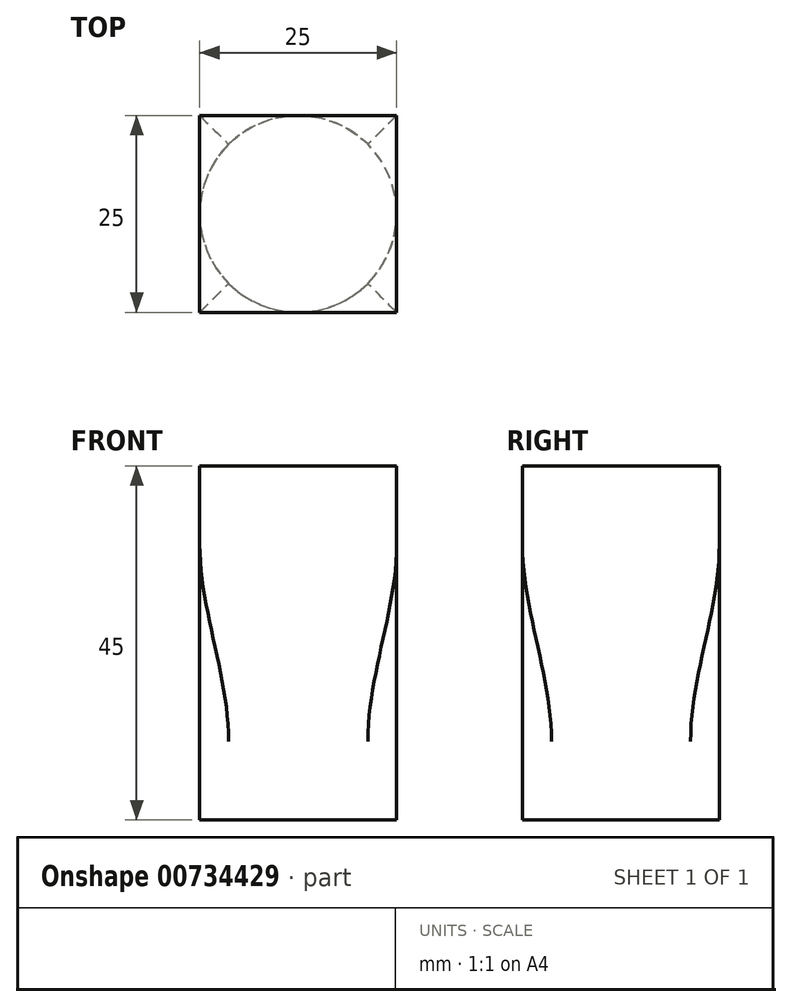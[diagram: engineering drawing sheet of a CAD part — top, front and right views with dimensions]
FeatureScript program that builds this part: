
annotation { "Feature Type Name" : "Feature", "Feature Type Description" : "" }
export const myFeature = defineFeature(function(context is Context, id is Id, definition is map)
    precondition{}
    {
        {
            var Q0;
            Q0=qCreatedBy(makeId("Top.planeOp"),FACE);
            cPlane(context, id + "F0", {"entities" : qUnion([Q0]), "cplaneType" : CPlaneType.OFFSET, "offset" : 25 * mm, "width" : 150 * mm, "height" : 150 * mm});
        }
        {
            var Q0;
            Q0=qCreatedBy(id+"F0.planeOp",FACE);
            var sketch = newSketch(context, id + "F1", { "sketchPlane" : qUnion([Q0])});
            skLineSegment(sketch, "E0.bottom", {"start": v(-12.5, -12.5) * mm, "end": v(12.5, -12.5) * mm});
            skLineSegment(sketch, "E0.top", {"start": v(-12.5, 12.5) * mm, "end": v(12.5, 12.5) * mm});
            skLineSegment(sketch, "E0.left", {"start": v(-12.5, -12.5) * mm, "end": v(-12.5, 12.5) * mm});
            skLineSegment(sketch, "E0.right", {"start": v(12.5, -12.5) * mm, "end": v(12.5, 12.5) * mm});
            skPoint(sketch, "E0.middle", {"position": v(0, 0) * mm});
            skSolve(sketch);
        }
        {
            var Q0;
            Q0=qCreatedBy(makeId("Top.planeOp"),FACE);
            var sketch = newSketch(context, id + "F2", { "sketchPlane" : qUnion([Q0])});
            skCircle(sketch, "E1", {"center": v(0, 0) * mm, "radius": 12.5 * mm});
            skSolve(sketch);
        }
        {
            var Q0;
            Q0=qSketchRegion(id+"F1",true);
            extrude(context, id + "F3", {"entities" : qUnion([Q0]), "depth" : 10 * mm, "offsetDistance" : 25 * mm});
        }
        {
            var Q0;
            Q0=qSketchRegion(id+"F2",true);
            extrude(context, id + "F4", {"entities" : qUnion([Q0]), "oppositeDirection" : true, "depth" : 10 * mm, "offsetDistance" : 25 * mm});
        }
        {
            var Q1;
            Q1=makeQuery(id+"F3.opExtrude","CAP_FACE",FACE,{"disambiguationData":[OSD([sQuery(id+"F1.wireOp",EDGE,"E0.bottom"),sQuery(id+"F1.wireOp",EDGE,"E0.top"),sQuery(id+"F1.wireOp",EDGE,"E0.left"),sQuery(id+"F1.wireOp",EDGE,"E0.right")])],"isStart":true});
            var Q2;
            Q2=makeQuery(id+"F4.opExtrude","CAP_FACE",FACE,{"disambiguationData":[OSD([sQuery(id+"F2.wireOp",EDGE,"E1")])],"isStart":true});
            loft(context, id + "F5", {"operationType" : NewBodyOperationType.ADD, "startCondition" : LoftEndDerivativeType.NORMAL_TO_PROFILE, "startMagnitude" : 1, "endCondition" : LoftEndDerivativeType.NORMAL_TO_PROFILE, "endMagnitude" : 1, "sheetProfilesArray" : [{ "sheetProfileEntities" : qUnion([Q1]) }, { "sheetProfileEntities" : qUnion([Q2]) }]});
        }
    });
